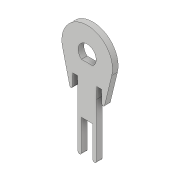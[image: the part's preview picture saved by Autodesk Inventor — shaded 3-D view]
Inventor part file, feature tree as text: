
AUTODESK INVENTOR PART (.ipt)
format: ipt  version: 2017 (Build 210142000, 142)  size: 198,656 bytes
history: native  units: in
note: dims shown in document units (in); Inventor stores cm internally (conversion verified against a paired STEP export)
features: sketch x5, extrude x3, projected_geometry x3, chamfer x2, sheet_metal_op x1, fillet x1, other x1
ambient origin geometry x8: Origin, YZ Plane, XZ Plane, XY Plane, X Axis, Y Axis, Z Axis, Center Point
bodies: Solid1 (feature_tree)
feature tree (16):
  sheet_metal_op  "Face1"
  extrude  "Extrusion1"  Depth=0.3937in
  sketch  "Sketch3"  dims[d10=0.25in d11=0.25in]
  fillet  "Fillet4"  Radius=0.5512in
  extrude  "Extrusion2"  Depth=0.0623in
  extrude  "Extrusion3"  Depth=0.25in
  chamfer  "Chamfer3"  Distance=1.0in
  chamfer  "Chamfer4"  Distance=0.0573in
  sketch  "Sketch1"  dims[d2=0.1969in d3=0.3937in d4=0.5512in]
  other  "Plate1"
  sketch  "Sketch2"  dims[d8=0.0623in d9=0.0623in]
  projected_geometry  "Projected Loop1"
  sketch  "Sketch4"  dims[d12=0.062in]
  projected_geometry  "Projected Loop2"
  sketch  "Sketch5"  dims[d14=0.125in d15=1.0in d16=0.0in d18=0.0573in d19=0.0573in d28=0.2362in d29=0.125in d30=0.2004in d31=0.1in d32=0.1in d33=0.0in d34=0.0179in d35=0.315in d36=0.0573in d37=0.015in d38=1.0in d39=0.0in d40=0.1969in d42=1.0in d43=0.0in d44=0.1752in d45=0.005in d46=0.125in d47=45.0deg d48=0.125in d49=0.005in d50=45.0deg]
  projected_geometry  "Projected Loop3"
